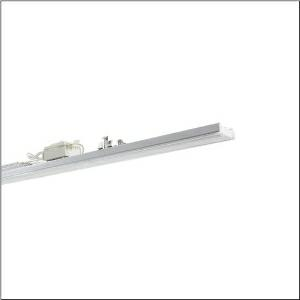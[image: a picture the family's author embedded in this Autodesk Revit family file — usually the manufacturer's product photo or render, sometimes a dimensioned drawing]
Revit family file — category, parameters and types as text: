
# Revit family: licross_r__11_recessed_ho_51tl11de47xs_07ca
name_source: partatom
category: Lighting Fixtures
units: mm (PartAtom-declared; Revit-internal decimal feet)

## family parameters
Cut with Voids When Loaded = No
Host = Face
Light Source = No
Part Type = Normal
Room Calculation Point = No
Round Connector Dimension = Use Diameter
Shared = No

## types (1)
- --- (1 x LED, 7000 lm, 40.2 W, 4000K)
    Apparent Load = 40 VA
    CIE Flux Codes = 87 95 99 100 100
    Color Rendering = 80
    Color Temperature = 4000K
    Default Elevation = 1800 mm
    Description = Licross® 11 Recessed HO, luminaire insert, of sheet steel, coil coated, white, length: 750mm, width: 66mm, height: 67mm, LED rated luminous flux: 7.000lm, light colour: 840, control gear: DALI 2, with plug, 5-pole, with phase selection, mains connection: 220..240V, AC, 50/60Hz, rated input power: 40W, halogen-free wiring, primary light control with lens, of plastic, primary optical cover: cover, of PMMA, light emission: direct distribution, primary light characteristic: symmetric, protection rating (complete): IP40, insulation class (complete): insulation class I (protective earthing), certification: CE, ENEC, VDE, UKCA, protection symbol: D if used in an environment without relevant dust loads with corresponding accessories, impact resistance: IK06, permissible ambient temperature for indoor applications: -25..+30°C, corresponds to IFS (International Featured Standards) requirements for safety and quality in the food industry, reducing of maximum allowable ambient temperature of 5°C with ceiling mounting, LABS conformity tested according to VDMA 24364:2018-05, packaging unit: 1 piece
    Height = 58 mm
    Lamp = 1 x LED
    Lamp Light Flux = 7000 lm
    Lamp Power = 40.2 W
    Lamp count = 1
    Length = 750 mm
    Luminous efficacy = 174 lm/W
    Manufacturer = Siteco
    ModVariant = No
    Model = 51TL11DE47XS
    Mounting Place = Ceiling
    Mounting Type = Pendant
    Number of Poles = 1
    OnlyDefault = Yes
    Power Factor = 1
    Product Name = Licross® 11 Recessed HO
    Product group = luminaire insert
    ProductGroupID = 902
    Protection Class = Protection class I
    Protection Degree = IP 40
    RLX_Detail_Level = 1
    RLX_Emergency_Light_Flux = 0 lm
    RLX_Emergency_Type = 0
    RLX_Emergency_Type_DB = No
    RlxData = <blob elided: 28837 chars, md5=fb7c8aca>
    Socket = socket
    Standby Power = 0 W
    System Light Flux = 7000 lm
    System Power = 40 W
    Type Comments = factory setting: luminous flux: 100 % | dim-lin: 254 | 522 mA
    Type Image = l_1296930.jpg
    URL = http://relux.com
    VarID = @adj_098782
    Voltage = 0 V
    Weight = 0.00 kg
    Width = 66 mm

## geometry (parser evidence)
native form markers: Blend x4, Sweep x10
no freeform markers — native parametric forms only
